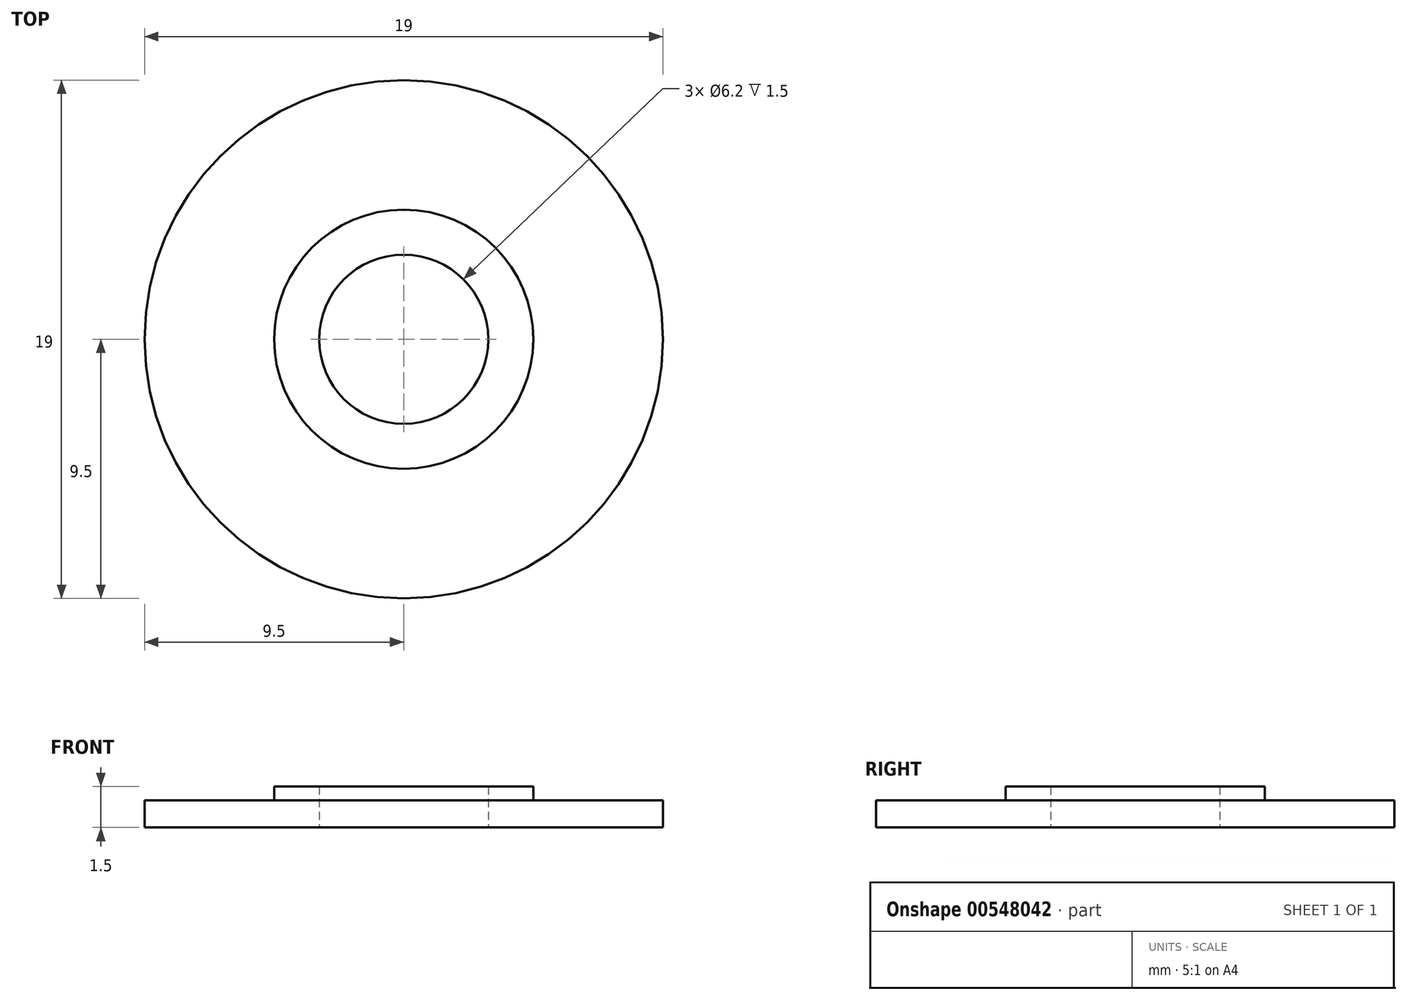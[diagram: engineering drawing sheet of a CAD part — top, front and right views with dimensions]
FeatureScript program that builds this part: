
annotation { "Feature Type Name" : "Feature", "Feature Type Description" : "" }
export const myFeature = defineFeature(function(context is Context, id is Id, definition is map)
    precondition{}
    {
        {
            var Q0;
            Q0=qCreatedBy(makeId("Front.planeOp"),FACE);
            var sketch = newSketch(context, id + "F0", { "sketchPlane" : qUnion([Q0])});
            skLineSegment(sketch, "E0", {"start": v(-9.5, 0) * mm, "end": v(-9.5, 1) * mm});
            skLineSegment(sketch, "E1", {"start": v(-9.5, 1) * mm, "end": v(-4.75, 1) * mm});
            skLineSegment(sketch, "E2", {"start": v(-4.75, 1) * mm, "end": v(-4.75, 1.5) * mm});
            skLineSegment(sketch, "E3", {"start": v(-4.75, 1.5) * mm, "end": v(-3.1, 1.5) * mm});
            skLineSegment(sketch, "E4", {"start": v(-3.1, 1.5) * mm, "end": v(-3.1, 0) * mm});
            skLineSegment(sketch, "E5", {"start": v(-3.1, 0) * mm, "end": v(-9.5, 0) * mm});
            skLineSegment(sketch, "E6", {"start": v(0, 0) * mm, "end": v(0, 4.82) * mm, "construction": true});
            skSolve(sketch);
        }
        {
            var Q0;
            Q0=makeQuery(id+"F0.imprint","IMPRINT",FACE,{"disambiguationData":[TD([[makeQuery(id+"F0.imprint","IMPRINT",EDGE,{"derivedFrom":sQuery(id+"F0.wireOp",EDGE,"E0")}),-1.0]])]});
            var Q1;
            Q1=sQuery(id+"F0.wireOp",EDGE,"E6");
            revolve(context, id + "F1", {"entities" : qUnion([Q0]), "axis" : qUnion([Q1]), "revolveType" : RevolveType.FULL});
        }
    });
